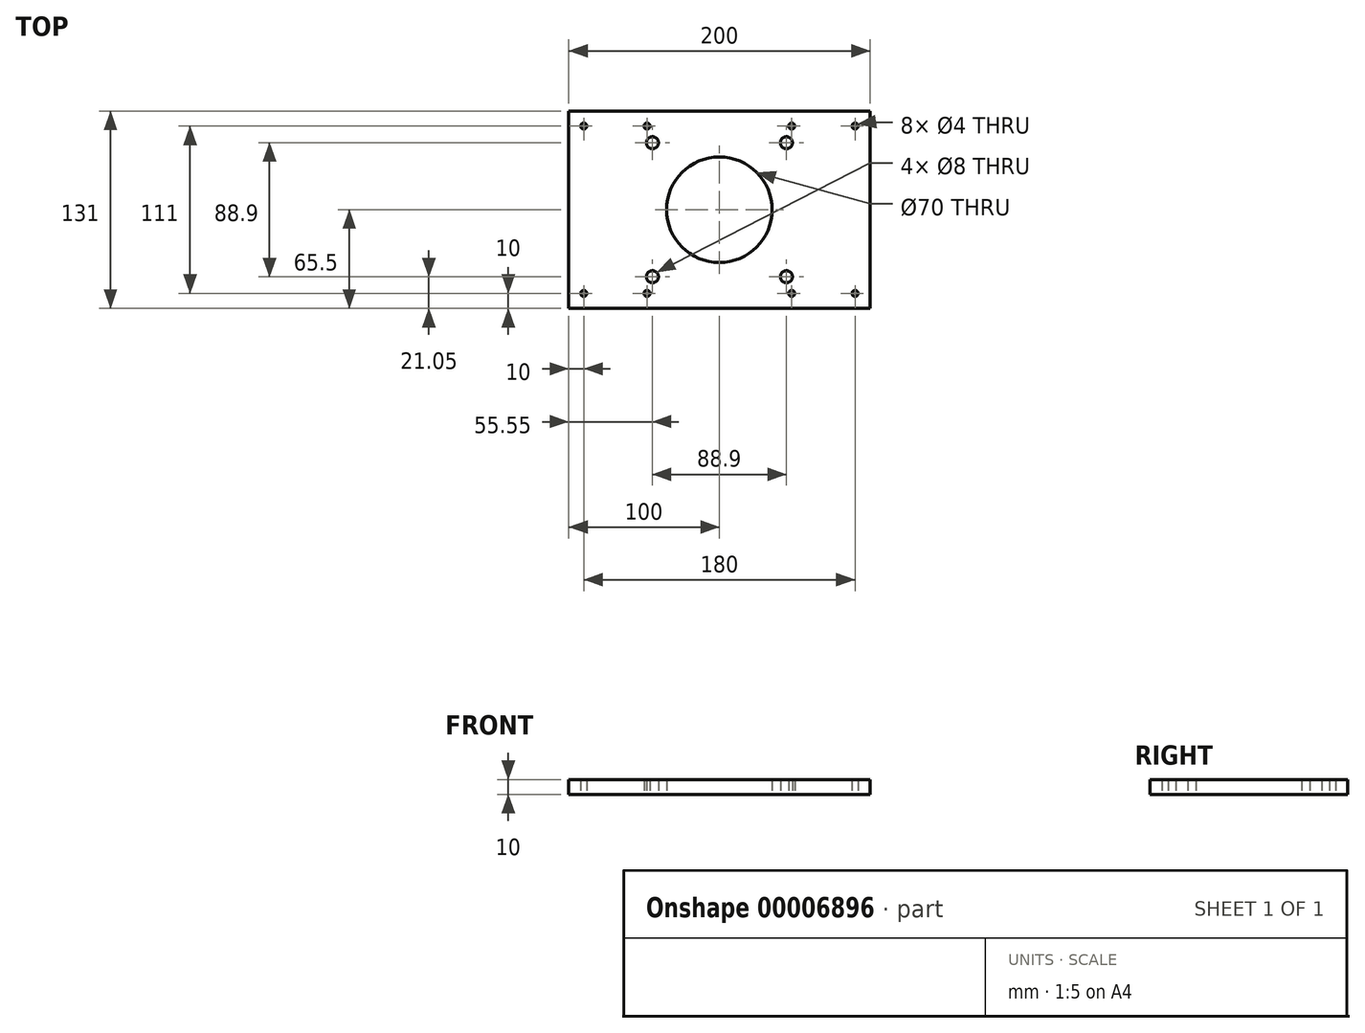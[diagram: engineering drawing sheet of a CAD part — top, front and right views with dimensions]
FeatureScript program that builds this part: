
annotation { "Feature Type Name" : "Feature", "Feature Type Description" : "" }
export const myFeature = defineFeature(function(context is Context, id is Id, definition is map)
    precondition{}
    {
        {
            var Q0;
            Q0=qCreatedBy(makeId("Top.planeOp"),FACE);
            var sketch = newSketch(context, id + "F0", { "sketchPlane" : qUnion([Q0])});
            skLineSegment(sketch, "E0.rect.bottom", {"start": v(100, -65.5) * mm, "end": v(-100, -65.5) * mm});
            skLineSegment(sketch, "E0.rect.top", {"start": v(100, 65.5) * mm, "end": v(-100, 65.5) * mm});
            skLineSegment(sketch, "E0.rect.left", {"start": v(100, -65.5) * mm, "end": v(100, 65.5) * mm});
            skLineSegment(sketch, "E0.rect.right", {"start": v(-100, -65.5) * mm, "end": v(-100, 65.5) * mm});
            skPoint(sketch, "E0.rect.middle", {"position": v(0, 0) * mm});
            skCircle(sketch, "E1", {"center": v(0, 0) * mm, "radius": 35 * mm});
            skCircle(sketch, "E2", {"center": v(-44.45, 44.45) * mm, "radius": 4 * mm});
            skCircle(sketch, "E3", {"center": v(44.45, 44.45) * mm, "radius": 4 * mm});
            skCircle(sketch, "E4", {"center": v(44.45, -44.45) * mm, "radius": 4 * mm});
            skCircle(sketch, "E5", {"center": v(-44.45, -44.45) * mm, "radius": 4 * mm});
            skCircle(sketch, "E6", {"center": v(-90, 55.5) * mm, "radius": 2 * mm});
            skCircle(sketch, "E7", {"center": v(-48, 55.5) * mm, "radius": 2 * mm});
            skCircle(sketch, "E8", {"center": v(-90, -55.5) * mm, "radius": 2 * mm});
            skCircle(sketch, "E9", {"center": v(-48, -55.5) * mm, "radius": 2 * mm});
            skCircle(sketch, "E10", {"center": v(90, -55.5) * mm, "radius": 2 * mm});
            skCircle(sketch, "E11", {"center": v(48, -55.5) * mm, "radius": 2 * mm});
            skCircle(sketch, "E12", {"center": v(90, 55.5) * mm, "radius": 2 * mm});
            skCircle(sketch, "E13", {"center": v(48, 55.5) * mm, "radius": 2 * mm});
            skLineSegment(sketch, "E14", {"start": v(-113, 0) * mm, "end": v(185, 0) * mm, "construction": true});
            skLineSegment(sketch, "E15", {"start": v(0, 88.94) * mm, "end": v(0, -137.61) * mm, "construction": true});
            skSolve(sketch);
        }
        {
            var Q0;
            Q0 = qSketchRegion(id + "F0", true);
            var Q1;
            Q1=makeQuery(id+"F0.imprint","IMPRINT",FACE,{"disambiguationData":[TD([[makeQuery(id+"F0.imprint","IMPRINT",EDGE,{"derivedFrom":sQuery(id+"F0.wireOp",EDGE,"E0.rect.bottom")}),-1.0]])]});
            extrude(context, id + "F1", {"entities" : qUnion([Q0, Q1]), "depth" : 10 * mm});
        }
    });
